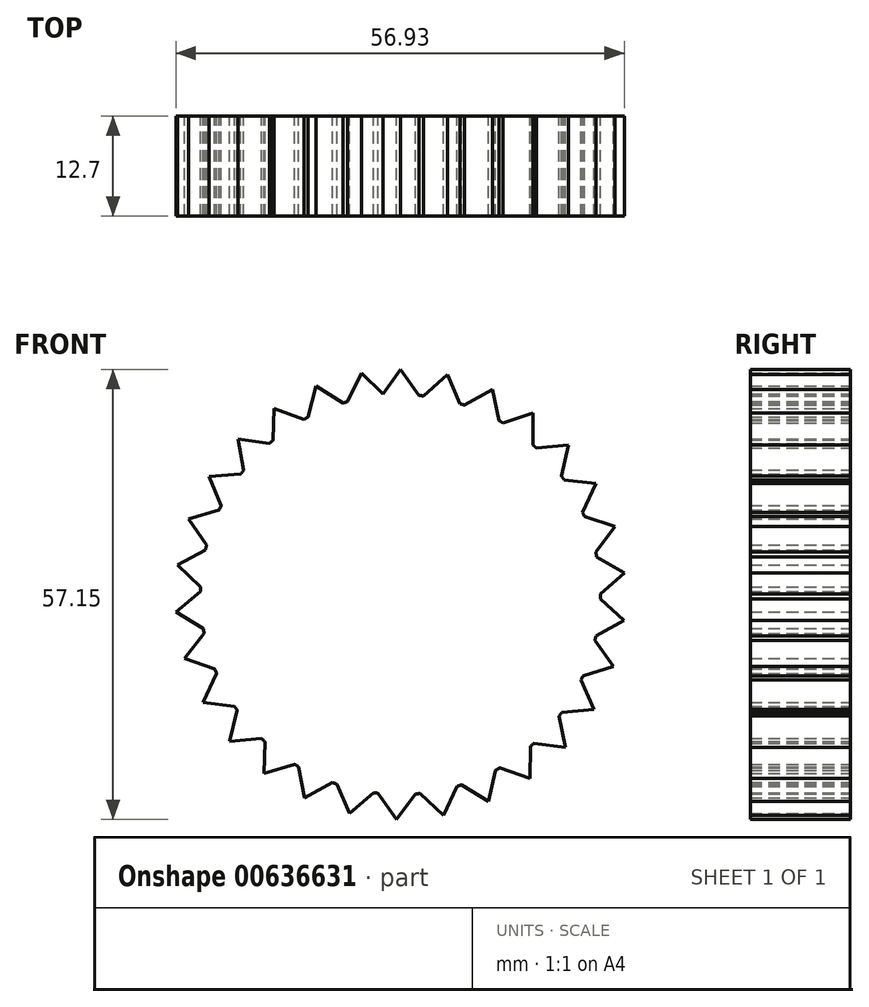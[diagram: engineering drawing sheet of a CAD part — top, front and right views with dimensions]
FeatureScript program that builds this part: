
annotation { "Feature Type Name" : "Feature", "Feature Type Description" : "" }
export const myFeature = defineFeature(function(context is Context, id is Id, definition is map)
    precondition{}
    {
        {
            var Q0;
            Q0=qCreatedBy(makeId("Front.planeOp"),FACE);
            var sketch = newSketch(context, id + "F0", { "sketchPlane" : qUnion([Q0])});
            skCircle(sketch, "E0", {"center": v(0, 0) * mm, "radius": 25.4 * mm});
            skLineSegment(sketch, "E1", {"start": v(0, 25.4) * mm, "end": v(0, 28.58) * mm, "construction": true});
            skLineSegment(sketch, "E2", {"start": v(0, 28.58) * mm, "end": v(-2.37, 25.29) * mm});
            skLineSegment(sketch, "E3.MirrorCS", {"start": v(0, 28.58) * mm, "end": v(2.37, 25.29) * mm});
            skLineSegment(sketch, "E4.1.0", {"start": v(5.97, 27.94) * mm, "end": v(2.97, 25.23) * mm});
            skLineSegment(sketch, "E4.1.1", {"start": v(5.97, 27.94) * mm, "end": v(7.6, 24.23) * mm});
            skLineSegment(sketch, "E4.2.0", {"start": v(11.69, 26.08) * mm, "end": v(8.18, 24.05) * mm});
            skLineSegment(sketch, "E4.2.1", {"start": v(11.69, 26.08) * mm, "end": v(12.5, 22.1) * mm});
            skLineSegment(sketch, "E4.3.0", {"start": v(16.88, 23.06) * mm, "end": v(13.03, 21.8) * mm});
            skLineSegment(sketch, "E4.3.1", {"start": v(16.88, 23.06) * mm, "end": v(16.85, 19) * mm});
            skLineSegment(sketch, "E4.4.0", {"start": v(21.33, 19.02) * mm, "end": v(17.3, 18.6) * mm});
            skLineSegment(sketch, "E4.4.1", {"start": v(21.33, 19.02) * mm, "end": v(20.45, 15.06) * mm});
            skLineSegment(sketch, "E4.5.0", {"start": v(24.83, 14.14) * mm, "end": v(20.8, 14.57) * mm});
            skLineSegment(sketch, "E4.5.1", {"start": v(24.83, 14.14) * mm, "end": v(23.15, 10.45) * mm});
            skLineSegment(sketch, "E4.6.0", {"start": v(27.24, 8.63) * mm, "end": v(23.4, 9.9) * mm});
            skLineSegment(sketch, "E4.6.1", {"start": v(27.24, 8.63) * mm, "end": v(24.82, 5.38) * mm});
            skLineSegment(sketch, "E4.7.0", {"start": v(28.44, 2.75) * mm, "end": v(24.94, 4.8) * mm});
            skLineSegment(sketch, "E4.7.1", {"start": v(28.44, 2.75) * mm, "end": v(25.4, 0.07) * mm});
            skLineSegment(sketch, "E4.8.0", {"start": v(28.39, -3.26) * mm, "end": v(25.4, -0.53) * mm});
            skLineSegment(sketch, "E4.8.1", {"start": v(28.39, -3.26) * mm, "end": v(24.85, -5.24) * mm});
            skLineSegment(sketch, "E4.9.0", {"start": v(27.08, -9.12) * mm, "end": v(24.72, -5.83) * mm});
            skLineSegment(sketch, "E4.9.1", {"start": v(27.08, -9.12) * mm, "end": v(23.2, -10.32) * mm});
            skLineSegment(sketch, "E4.10.0", {"start": v(24.57, -14.58) * mm, "end": v(22.96, -10.87) * mm});
            skLineSegment(sketch, "E4.10.1", {"start": v(24.57, -14.58) * mm, "end": v(20.54, -14.95) * mm});
            skLineSegment(sketch, "E4.11.0", {"start": v(20.98, -19.4) * mm, "end": v(20.18, -15.43) * mm});
            skLineSegment(sketch, "E4.11.1", {"start": v(20.98, -19.4) * mm, "end": v(16.96, -18.9) * mm});
            skLineSegment(sketch, "E4.12.0", {"start": v(16.46, -23.36) * mm, "end": v(16.5, -19.3) * mm});
            skLineSegment(sketch, "E4.12.1", {"start": v(16.46, -23.36) * mm, "end": v(12.63, -22.04) * mm});
            skLineSegment(sketch, "E4.13.0", {"start": v(11.21, -26.28) * mm, "end": v(12.1, -22.33) * mm});
            skLineSegment(sketch, "E4.13.1", {"start": v(11.21, -26.28) * mm, "end": v(7.74, -24.2) * mm});
            skLineSegment(sketch, "E4.14.0", {"start": v(5.47, -28.05) * mm, "end": v(7.17, -24.37) * mm});
            skLineSegment(sketch, "E4.14.1", {"start": v(5.47, -28.05) * mm, "end": v(2.51, -25.28) * mm});
            skLineSegment(sketch, "E4.15.0", {"start": v(-0.52, -28.57) * mm, "end": v(1.91, -25.33) * mm});
            skLineSegment(sketch, "E4.15.1", {"start": v(-0.52, -28.57) * mm, "end": v(-2.83, -25.24) * mm});
            skLineSegment(sketch, "E4.16.0", {"start": v(-6.48, -27.83) * mm, "end": v(-3.43, -25.17) * mm});
            skLineSegment(sketch, "E4.16.1", {"start": v(-6.48, -27.83) * mm, "end": v(-8.04, -24.1) * mm});
            skLineSegment(sketch, "E4.17.0", {"start": v(-12.15, -25.86) * mm, "end": v(-8.61, -23.9) * mm});
            skLineSegment(sketch, "E4.17.1", {"start": v(-12.15, -25.86) * mm, "end": v(-12.9, -21.88) * mm});
            skLineSegment(sketch, "E4.18.0", {"start": v(-17.3, -22.75) * mm, "end": v(-13.42, -21.57) * mm});
            skLineSegment(sketch, "E4.18.1", {"start": v(-17.3, -22.75) * mm, "end": v(-17.2, -18.7) * mm});
            skLineSegment(sketch, "E4.19.0", {"start": v(-21.67, -18.63) * mm, "end": v(-17.63, -18.28) * mm});
            skLineSegment(sketch, "E4.19.1", {"start": v(-21.67, -18.63) * mm, "end": v(-20.72, -14.7) * mm});
            skLineSegment(sketch, "E4.20.0", {"start": v(-25.08, -13.69) * mm, "end": v(-21.06, -14.2) * mm});
            skLineSegment(sketch, "E4.20.1", {"start": v(-25.08, -13.69) * mm, "end": v(-23.33, -10.03) * mm});
            skLineSegment(sketch, "E4.21.0", {"start": v(-27.4, -8.14) * mm, "end": v(-23.57, -9.48) * mm});
            skLineSegment(sketch, "E4.21.1", {"start": v(-27.4, -8.14) * mm, "end": v(-24.92, -4.93) * mm});
            skLineSegment(sketch, "E4.22.0", {"start": v(-28.49, -2.23) * mm, "end": v(-25.03, -4.34) * mm});
            skLineSegment(sketch, "E4.22.1", {"start": v(-28.49, -2.23) * mm, "end": v(-25.4, 0.39) * mm});
            skLineSegment(sketch, "E4.23.0", {"start": v(-28.32, 3.77) * mm, "end": v(-25.38, 0.99) * mm});
            skLineSegment(sketch, "E4.23.1", {"start": v(-28.32, 3.77) * mm, "end": v(-24.76, 5.69) * mm});
            skLineSegment(sketch, "E4.24.0", {"start": v(-26.91, 9.61) * mm, "end": v(-24.61, 6.27) * mm});
            skLineSegment(sketch, "E4.24.1", {"start": v(-26.91, 9.61) * mm, "end": v(-23.02, 10.74) * mm});
            skLineSegment(sketch, "E4.25.0", {"start": v(-24.3, 15.03) * mm, "end": v(-22.76, 11.28) * mm});
            skLineSegment(sketch, "E4.25.1", {"start": v(-24.3, 15.03) * mm, "end": v(-20.26, 15.31) * mm});
            skLineSegment(sketch, "E4.26.0", {"start": v(-20.63, 19.78) * mm, "end": v(-19.9, 15.8) * mm});
            skLineSegment(sketch, "E4.26.1", {"start": v(-20.63, 19.78) * mm, "end": v(-16.61, 19.21) * mm});
            skLineSegment(sketch, "E4.27.0", {"start": v(-16.04, 23.65) * mm, "end": v(-16.15, 19.6) * mm});
            skLineSegment(sketch, "E4.27.1", {"start": v(-16.04, 23.65) * mm, "end": v(-12.23, 22.26) * mm});
            skLineSegment(sketch, "E4.28.0", {"start": v(-10.74, 26.48) * mm, "end": v(-11.7, 22.55) * mm});
            skLineSegment(sketch, "E4.28.1", {"start": v(-10.74, 26.48) * mm, "end": v(-7.3, 24.33) * mm});
            skLineSegment(sketch, "E4.29.0", {"start": v(-4.96, 28.14) * mm, "end": v(-6.73, 24.5) * mm});
            skLineSegment(sketch, "E4.29.1", {"start": v(-4.96, 28.14) * mm, "end": v(-2.06, 25.32) * mm});
            skLineSegment(sketch, "E4.anchor1", {"start": v(0, 0) * mm, "end": v(-2.37, 25.29) * mm, "construction": true});
            skLineSegment(sketch, "E4.anchor2", {"start": v(0, 0) * mm, "end": v(-6.73, 24.5) * mm, "construction": true});
            skSolve(sketch);
        }
        {
            var Q0;
            Q0 = qSketchRegion(id + "F0", true);
            extrude(context, id + "F1", {"entities" : qUnion([Q0]), "depth" : 12.7 * mm, "offsetDistance" : 25.4 * mm});
        }
    });
